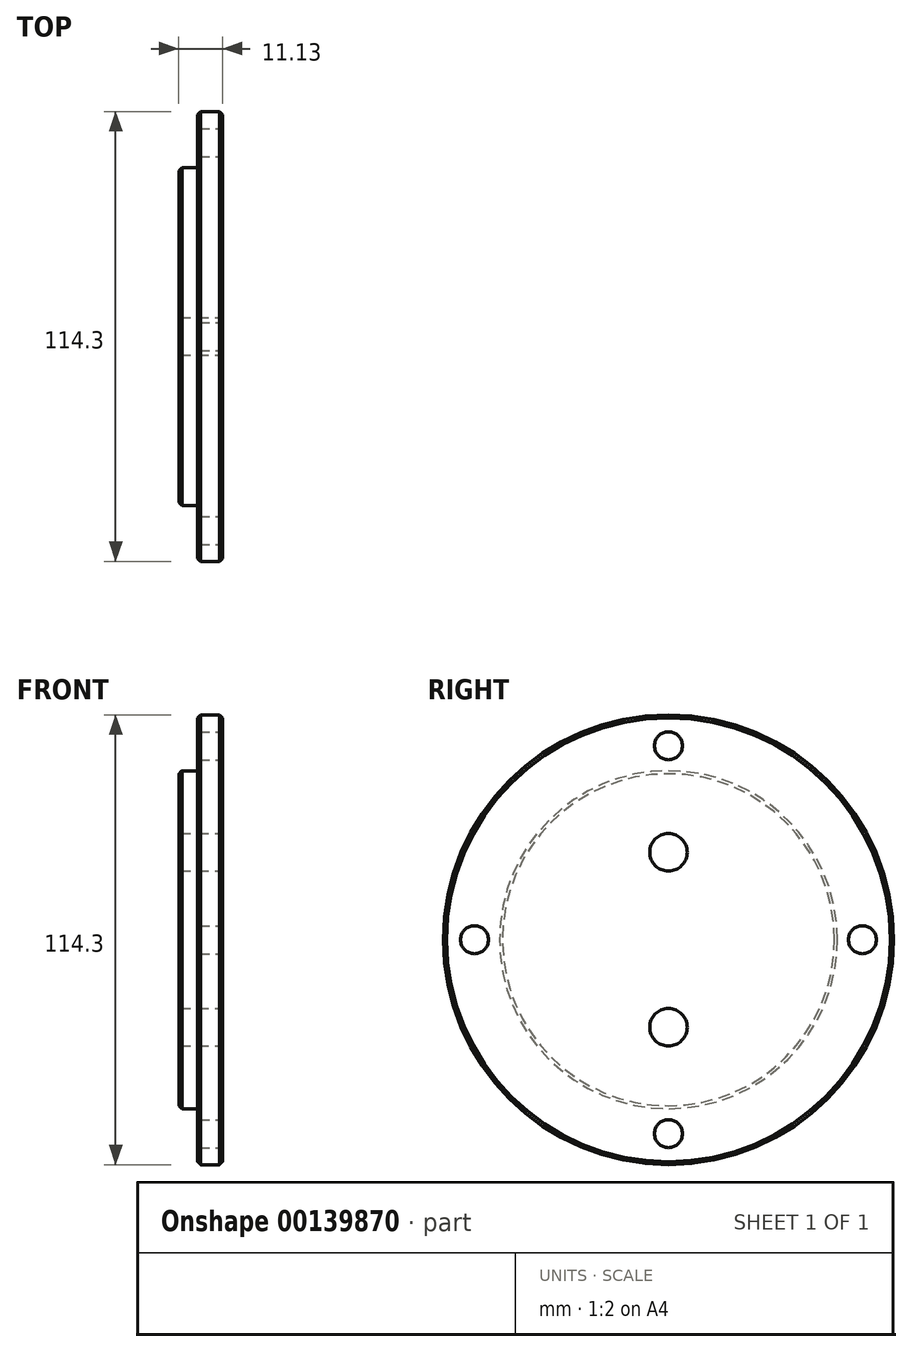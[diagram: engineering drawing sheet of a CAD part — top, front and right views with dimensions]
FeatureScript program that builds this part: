
annotation { "Feature Type Name" : "Feature", "Feature Type Description" : "" }
export const myFeature = defineFeature(function(context is Context, id is Id, definition is map)
    precondition{}
    {
        {
            var Q0;
            Q0=qCreatedBy(makeId("Right.planeOp"),FACE);
            var sketch = newSketch(context, id + "F0", { "sketchPlane" : qUnion([Q0])});
            skCircle(sketch, "E0", {"center": v(0, 0) * mm, "radius": 57.15 * mm});
            skSolve(sketch);
        }
        {
            var Q0;
            Q0=qSketchRegion(id+"F0",true);
            extrude(context, id + "F1", {"entities" : qUnion([Q0]), "depth" : 6.35 * mm});
        }
        {
            var Q0;
            Q0=makeQuery(id+"F1.opExtrude","CAP_FACE",FACE,{"disambiguationData":[OSD([sQuery(id+"F0.wireOp",EDGE,"E0")])],"isStart":true});
            var sketch = newSketch(context, id + "F2", { "sketchPlane" : qUnion([Q0])});
            skCircle(sketch, "E1", {"center": v(0, 0) * mm, "radius": 42.93 * mm});
            skSolve(sketch);
        }
        {
            var Q0;
            Q0=qSketchRegion(id+"F2",true);
            extrude(context, id + "F3", {"entities" : qUnion([Q0]), "operationType" : NewBodyOperationType.ADD, "depth" : 4.78 * mm});
        }
        {
            var Q0;
            Q0=makeQuery(id+"F1.opExtrude","CAP_EDGE",EDGE,{"disambiguationData":[OSD([sQuery(id+"F0.wireOp",EDGE,"E0")])],"isStart":false});
            var Q1;
            Q1=makeQuery(id+"F1.opExtrude","CAP_EDGE",EDGE,{"disambiguationData":[OSD([sQuery(id+"F0.wireOp",EDGE,"E0")])],"isStart":true});
            var Q2;
            Q2=makeQuery(id+"F3.opExtrude","CAP_EDGE",EDGE,{"disambiguationData":[OSD([sQuery(id+"F2.wireOp",EDGE,"E1")])],"isStart":false});
            chamfer(context, id + "F4", {"entities" : qUnion([Q0, Q1, Q2]), "width" : 0.76 * mm, "tangentPropagation" : true});
        }
        {
            var Q0;
            Q0=makeQuery(id+"F1.opExtrude","CAP_FACE",FACE,{"disambiguationData":[OSD([sQuery(id+"F0.wireOp",EDGE,"E0")])],"isStart":false});
            var sketch = newSketch(context, id + "F5", { "sketchPlane" : qUnion([Q0])});
            skCircle(sketch, "E2", {"center": v(0, 0) * mm, "radius": 49.28 * mm, "construction": true});
            skLineSegment(sketch, "E3", {"start": v(0, 0) * mm, "end": v(0, 77.99) * mm, "construction": true});
            skPoint(sketch, "E4", {"position": v(0, 49.28) * mm});
            skPoint(sketch, "E5.1.0", {"position": v(-49.28, 0) * mm});
            skPoint(sketch, "E5.2.0", {"position": v(0, -49.28) * mm});
            skPoint(sketch, "E5.3.0", {"position": v(49.28, 0) * mm});
            skSolve(sketch);
        }
        {
            var Q0;
            Q0=sQuery(id+"F5.wireOp",VERTEX,"E4");
            var Q1;
            Q1=sQuery(id+"F5.wireOp",VERTEX,"E5.3.0");
            var Q2;
            Q2=sQuery(id+"F5.wireOp",VERTEX,"E5.2.0");
            var Q3;
            Q3=sQuery(id+"F5.wireOp",VERTEX,"E5.1.0");
            var Q4;
            Q4=makeQuery(id+"F1.opExtrude","SWEPT_BODY",BODY,{"disambiguationData":[OSD([sQuery(id+"F0.wireOp",EDGE,"E0")])]});
            hole(context, id + "F6", {"style" : HoleStyle.SIMPLE, "holeDiameter" : 7.11 * mm, "endStyle" : HoleEndStyle.THROUGH, "locations" : qUnion([Q0, Q1, Q2, Q3]), "scope" : qUnion([Q4])});
        }
        {
            var Q0;
            Q0=makeQuery(id+"F1.opExtrude","CAP_FACE",FACE,{"disambiguationData":[OSD([sQuery(id+"F0.wireOp",EDGE,"E0")])],"isStart":false});
            var sketch = newSketch(context, id + "F7", { "sketchPlane" : qUnion([Q0])});
            skCircle(sketch, "E6", {"center": v(0, 0) * mm, "radius": 22.23 * mm, "construction": true});
            skLineSegment(sketch, "E7", {"start": v(0, 0) * mm, "end": v(0, 90.71) * mm, "construction": true});
            skPoint(sketch, "E8", {"position": v(0, 22.23) * mm});
            skPoint(sketch, "E9.1.0", {"position": v(0, -22.23) * mm});
            skSolve(sketch);
        }
        {
            var Q0;
            Q0=sQuery(id+"F7.wireOp",VERTEX,"E8");
            var Q1;
            Q1=sQuery(id+"F7.wireOp",VERTEX,"E9.1.0");
            var Q2;
            Q2=makeQuery(id+"F1.opExtrude","SWEPT_BODY",BODY,{"disambiguationData":[OSD([sQuery(id+"F0.wireOp",EDGE,"E0")])]});
            hole(context, id + "F8", {"style" : HoleStyle.SIMPLE, "holeDiameter" : 9.52 * mm, "endStyle" : HoleEndStyle.THROUGH, "locations" : qUnion([Q0, Q1]), "scope" : qUnion([Q2])});
        }
    });
